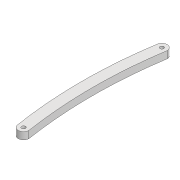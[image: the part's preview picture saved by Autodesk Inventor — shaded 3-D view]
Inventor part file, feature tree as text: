
AUTODESK INVENTOR PART (.ipt)
format: ipt  version: 2022 (Build 260153000, 153)  size: 92,672 bytes
history: native  units: mm
features: extrude x1, sketch x1
ambient origin geometry x8: Origin, YZ Plane, XZ Plane, XY Plane, X Axis, Y Axis, Z Axis, Center Point
bodies: Solid1 (feature_tree)
feature tree (2):
  extrude  "Extrusion1"  Depth=250.0mm
  sketch  "Sketch1"  dims[d0=2.2mm d1=2.2mm d2=6.0mm d3=77.772mm d6=4.0mm d7=0.0mm d12=250.0mm d13=250.0mm]
